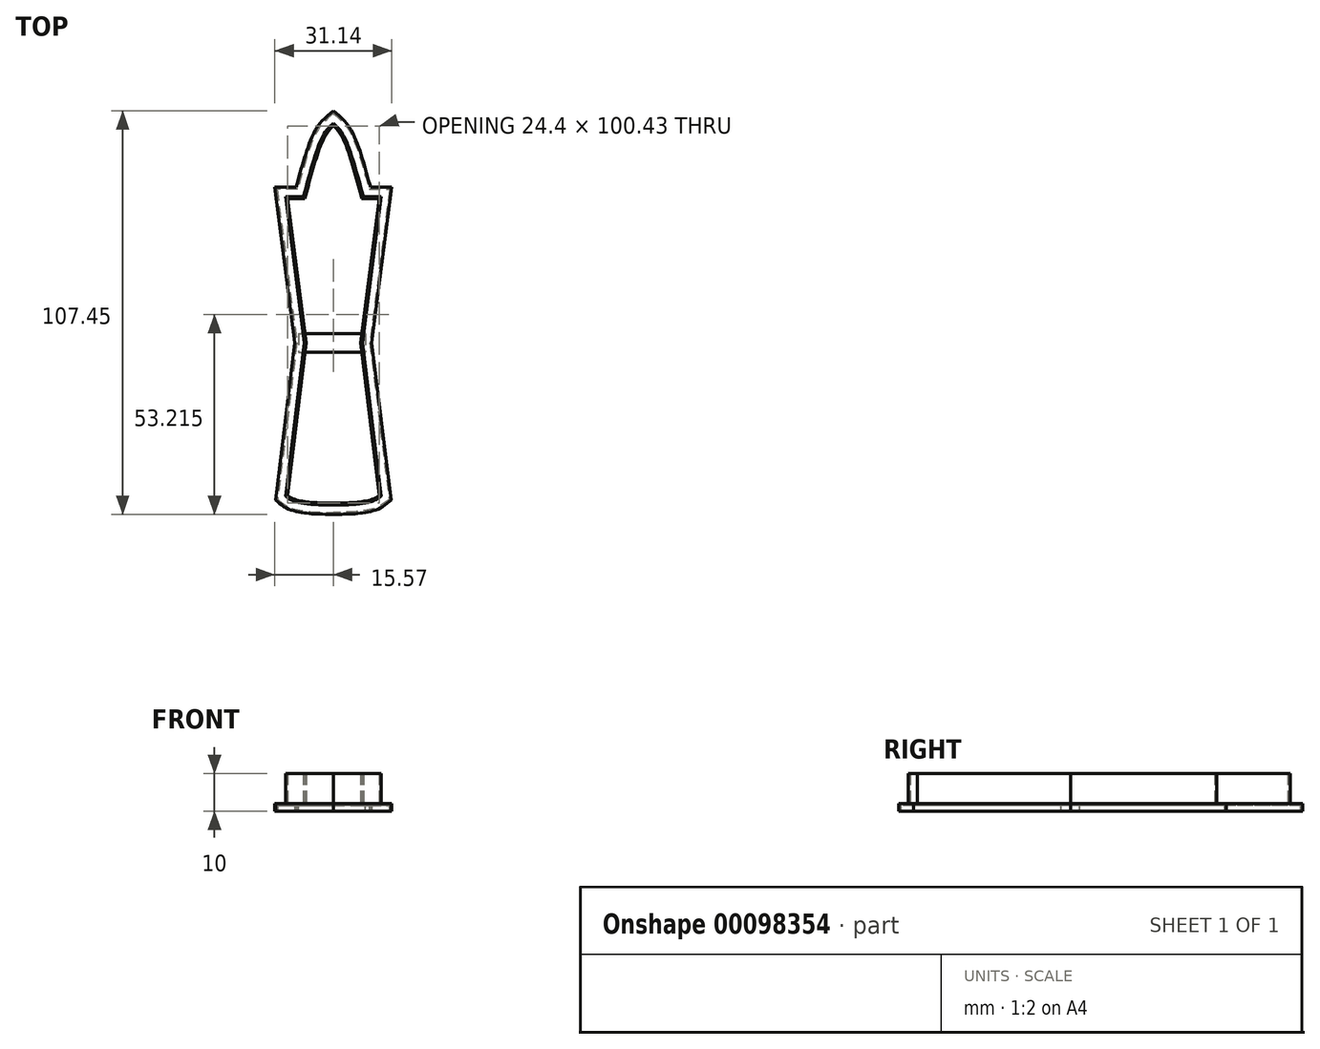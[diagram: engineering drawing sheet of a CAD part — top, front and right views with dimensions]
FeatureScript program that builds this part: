
annotation { "Feature Type Name" : "Feature", "Feature Type Description" : "" }
export const myFeature = defineFeature(function(context is Context, id is Id, definition is map)
    precondition{}
    {
        {
            var Q0;
            Q0=qCreatedBy(makeId("Top.planeOp"),FACE);
            var sketch = newSketch(context, id + "F0", { "sketchPlane" : qUnion([Q0])});
            skFitSpline(sketch, "E0", {"points": [v(0, 0) * mm, v(-2.69, -3.2) * mm, v(-7.96, -19.52) * mm], "startDerivative": vector(-8.18, -7.27) * mm, "endDerivative": vector(-7.79, -29.29) * mm});
            skLineSegment(sketch, "E1", {"start": v(-7.96, -19.52) * mm, "end": v(-12.73, -19.52) * mm});
            skLineSegment(sketch, "E2", {"start": v(-12.73, -19.52) * mm, "end": v(-7.7, -58.42) * mm});
            skLineSegment(sketch, "E3", {"start": v(-7.7, -58.42) * mm, "end": v(-12.73, -99.25) * mm});
            skFitSpline(sketch, "E4", {"points": [v(-12.73, -99.25) * mm, v(-8.63, -101.03) * mm, v(0, -101.6) * mm], "startDerivative": vector(9.98, -8.62) * mm, "endDerivative": vector(28.05, -0.37) * mm});
            skLineSegment(sketch, "E5", {"start": v(0, 0) * mm, "end": v(0, -101.6) * mm, "construction": true});
            skFitSpline(sketch, "E6.MirrorCS", {"points": [v(0, 0) * mm, v(2.69, -3.2) * mm, v(7.96, -19.52) * mm], "startDerivative": vector(8.18, -7.27) * mm, "endDerivative": vector(7.79, -29.29) * mm});
            skLineSegment(sketch, "E7.MirrorCS", {"start": v(7.96, -19.52) * mm, "end": v(12.73, -19.52) * mm});
            skLineSegment(sketch, "E8.MirrorCS", {"start": v(12.73, -19.52) * mm, "end": v(7.7, -58.42) * mm});
            skLineSegment(sketch, "E9.MirrorCS", {"start": v(7.7, -58.42) * mm, "end": v(12.73, -99.25) * mm});
            skFitSpline(sketch, "E10.MirrorCS", {"points": [v(12.73, -99.25) * mm, v(8.63, -101.03) * mm, v(0, -101.6) * mm], "startDerivative": vector(-9.98, -8.62) * mm, "endDerivative": vector(-28.05, -0.37) * mm});
            skLineSegment(sketch, "E11", {"start": v(12.73, -19.52) * mm, "end": v(12.73, -119.48) * mm, "construction": true});
            skSolve(sketch);
        }
        {
            var Q0;
            Q0 = qSketchRegion(id + "F0", true);
            extrude(context, id + "F1", {"entities" : qUnion([Q0]), "depth" : 2 * mm});
        }
        {
            var Q0;
            Q0=makeQuery(id+"F1.opExtrude","SWEPT_BODY",BODY,{"disambiguationData":[OSD([sQuery(id+"F0.wireOp",EDGE,"E0"),sQuery(id+"F0.wireOp",EDGE,"E1"),sQuery(id+"F0.wireOp",EDGE,"E2"),sQuery(id+"F0.wireOp",EDGE,"E3"),sQuery(id+"F0.wireOp",EDGE,"E4"),sQuery(id+"F0.wireOp",EDGE,"E6.MirrorCS"),sQuery(id+"F0.wireOp",EDGE,"E7.MirrorCS"),sQuery(id+"F0.wireOp",EDGE,"E8.MirrorCS"),sQuery(id+"F0.wireOp",EDGE,"E9.MirrorCS"),sQuery(id+"F0.wireOp",EDGE,"E10.MirrorCS")])]});
            transform(context, id + "F2", {"entities" : qUnion([Q0]), "transformType" : TransformType.TRANSLATION_3D, "dx" : 0 * mm, "dy" : 0 * mm, "dz" : 0 * mm, "makeCopy" : true});
        }
        {
            var Q0;
            Q0=makeQuery(id+"F1.opExtrude","CAP_FACE",FACE,{"disambiguationData":[OSD([sQuery(id+"F0.wireOp",EDGE,"E0"),sQuery(id+"F0.wireOp",EDGE,"E1"),sQuery(id+"F0.wireOp",EDGE,"E2"),sQuery(id+"F0.wireOp",EDGE,"E3"),sQuery(id+"F0.wireOp",EDGE,"E4"),sQuery(id+"F0.wireOp",EDGE,"E6.MirrorCS"),sQuery(id+"F0.wireOp",EDGE,"E7.MirrorCS"),sQuery(id+"F0.wireOp",EDGE,"E8.MirrorCS"),sQuery(id+"F0.wireOp",EDGE,"E9.MirrorCS"),sQuery(id+"F0.wireOp",EDGE,"E10.MirrorCS")])],"isStart":true});
            var Q1;
            Q1=makeQuery(id+"F1.opExtrude","CAP_FACE",FACE,{"disambiguationData":[OSD([sQuery(id+"F0.wireOp",EDGE,"E0"),sQuery(id+"F0.wireOp",EDGE,"E1"),sQuery(id+"F0.wireOp",EDGE,"E2"),sQuery(id+"F0.wireOp",EDGE,"E3"),sQuery(id+"F0.wireOp",EDGE,"E4"),sQuery(id+"F0.wireOp",EDGE,"E6.MirrorCS"),sQuery(id+"F0.wireOp",EDGE,"E7.MirrorCS"),sQuery(id+"F0.wireOp",EDGE,"E8.MirrorCS"),sQuery(id+"F0.wireOp",EDGE,"E9.MirrorCS"),sQuery(id+"F0.wireOp",EDGE,"E10.MirrorCS")])],"isStart":false});
            shell(context, id + "F3", {"entities" : qUnion([Q0, Q1]), "thickness" : 2.5 * mm, "oppositeDirection" : true});
        }
        {
            var Q0;
            Q0=makeQuery(id+"F2.opPattern","COPY",FACE,{"derivedFrom":makeQuery(id+"F1.opExtrude","CAP_FACE",FACE,{"disambiguationData":[OSD([sQuery(id+"F0.wireOp",EDGE,"E0"),sQuery(id+"F0.wireOp",EDGE,"E1"),sQuery(id+"F0.wireOp",EDGE,"E2"),sQuery(id+"F0.wireOp",EDGE,"E3"),sQuery(id+"F0.wireOp",EDGE,"E4"),sQuery(id+"F0.wireOp",EDGE,"E6.MirrorCS"),sQuery(id+"F0.wireOp",EDGE,"E7.MirrorCS"),sQuery(id+"F0.wireOp",EDGE,"E8.MirrorCS"),sQuery(id+"F0.wireOp",EDGE,"E9.MirrorCS"),sQuery(id+"F0.wireOp",EDGE,"E10.MirrorCS")])],"isStart":false}),"instanceName":"1"});
            extrude(context, id + "F4", {"entities" : qUnion([Q0]), "operationType" : NewBodyOperationType.ADD, "depth" : 8 * mm});
        }
        {
            var Q0;
            Q0=makeQuery(id+"F4.opExtrude","CAP_FACE",FACE,{"disambiguationData":[OSD([sQuery(id+"F0.wireOp",EDGE,"E0"),sQuery(id+"F0.wireOp",EDGE,"E1"),sQuery(id+"F0.wireOp",EDGE,"E2"),sQuery(id+"F0.wireOp",EDGE,"E3"),sQuery(id+"F0.wireOp",EDGE,"E4"),sQuery(id+"F0.wireOp",EDGE,"E6.MirrorCS"),sQuery(id+"F0.wireOp",EDGE,"E7.MirrorCS"),sQuery(id+"F0.wireOp",EDGE,"E8.MirrorCS"),sQuery(id+"F0.wireOp",EDGE,"E9.MirrorCS"),sQuery(id+"F0.wireOp",EDGE,"E10.MirrorCS")])],"isStart":false});
            var Q1;
            Q1=makeQuery(id+"F2.opPattern","COPY",FACE,{"derivedFrom":makeQuery(id+"F1.opExtrude","CAP_FACE",FACE,{"disambiguationData":[OSD([sQuery(id+"F0.wireOp",EDGE,"E0"),sQuery(id+"F0.wireOp",EDGE,"E1"),sQuery(id+"F0.wireOp",EDGE,"E2"),sQuery(id+"F0.wireOp",EDGE,"E3"),sQuery(id+"F0.wireOp",EDGE,"E4"),sQuery(id+"F0.wireOp",EDGE,"E6.MirrorCS"),sQuery(id+"F0.wireOp",EDGE,"E7.MirrorCS"),sQuery(id+"F0.wireOp",EDGE,"E8.MirrorCS"),sQuery(id+"F0.wireOp",EDGE,"E9.MirrorCS"),sQuery(id+"F0.wireOp",EDGE,"E10.MirrorCS")])],"isStart":true}),"instanceName":"1"});
            shell(context, id + "F5", {"entities" : qUnion([Q0, Q1]), "thickness" : .5 * mm});
        }
        {
            var Q0;
            Q0=makeQuery(id+"F1.opExtrude","CAP_FACE",FACE,{"disambiguationData":[OSD([sQuery(id+"F0.wireOp",EDGE,"E0"),sQuery(id+"F0.wireOp",EDGE,"E1"),sQuery(id+"F0.wireOp",EDGE,"E2"),sQuery(id+"F0.wireOp",EDGE,"E3"),sQuery(id+"F0.wireOp",EDGE,"E4"),sQuery(id+"F0.wireOp",EDGE,"E6.MirrorCS"),sQuery(id+"F0.wireOp",EDGE,"E7.MirrorCS"),sQuery(id+"F0.wireOp",EDGE,"E8.MirrorCS"),sQuery(id+"F0.wireOp",EDGE,"E9.MirrorCS"),sQuery(id+"F0.wireOp",EDGE,"E10.MirrorCS")])],"isStart":false});
            var sketch = newSketch(context, id + "F6", { "sketchPlane" : qUnion([Q0])});
            skLineSegment(sketch, "E12.bottom", {"start": v(-9.24, -55.97) * mm, "end": v(8.51, -55.97) * mm});
            skLineSegment(sketch, "E12.top", {"start": v(-9.24, -60.97) * mm, "end": v(8.51, -60.97) * mm});
            skLineSegment(sketch, "E12.left", {"start": v(-9.24, -55.97) * mm, "end": v(-9.24, -60.97) * mm});
            skLineSegment(sketch, "E12.right", {"start": v(8.51, -55.97) * mm, "end": v(8.51, -60.97) * mm});
            skSolve(sketch);
        }
        {
            var Q0;
            Q0 = qSketchRegion(id + "F6", true);
            extrude(context, id + "F7", {"entities" : qUnion([Q0]), "operationType" : NewBodyOperationType.ADD, "oppositeDirection" : true, "depth" : 2 * mm});
        }
    });
